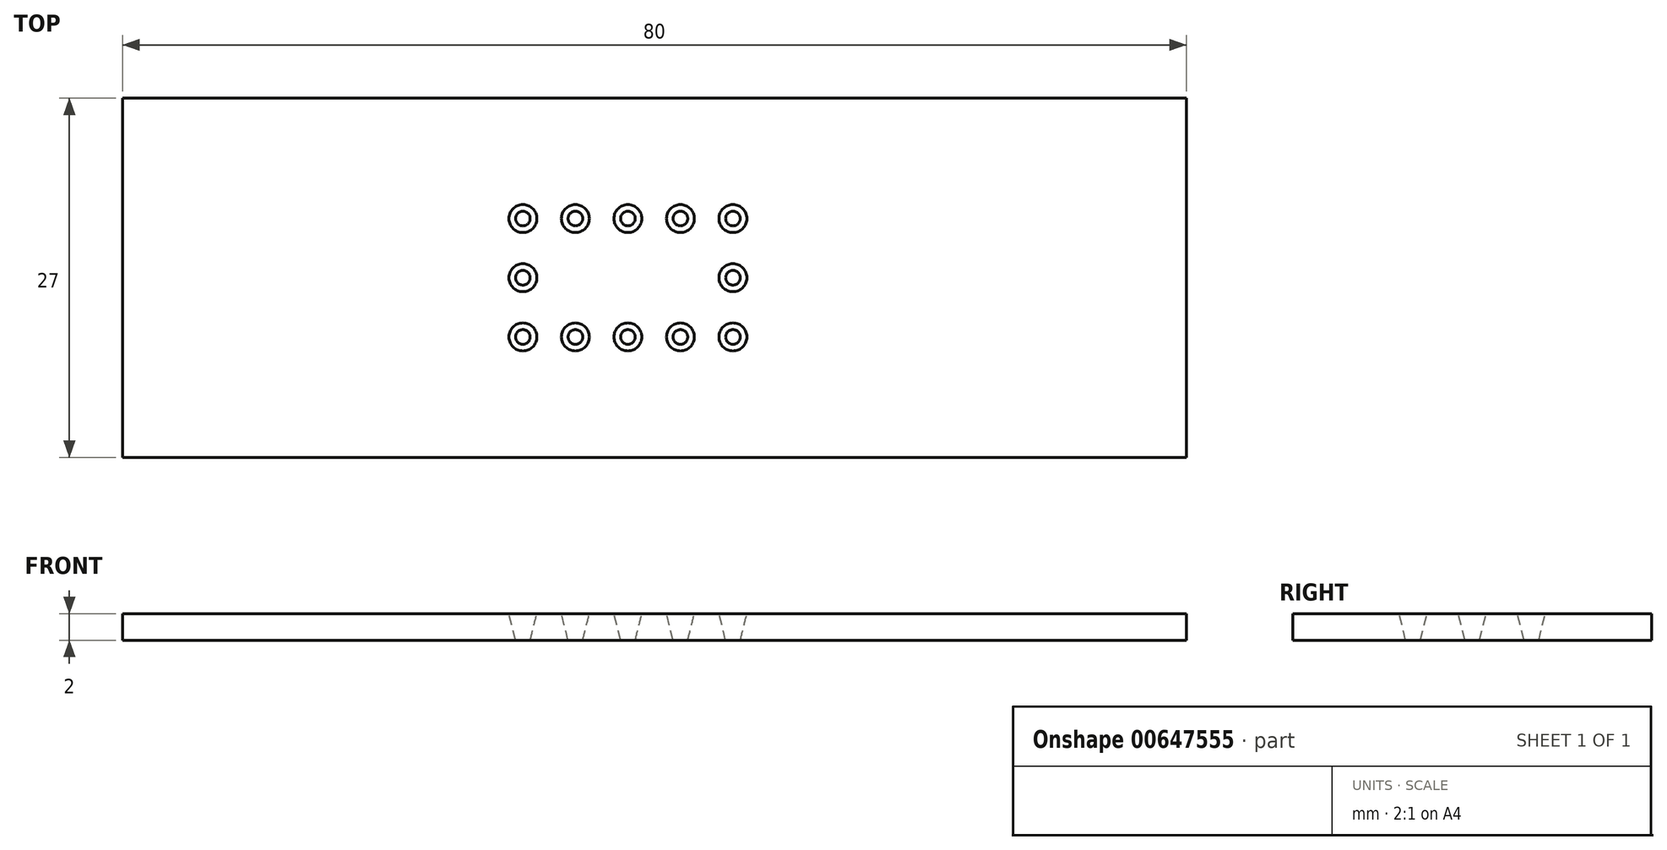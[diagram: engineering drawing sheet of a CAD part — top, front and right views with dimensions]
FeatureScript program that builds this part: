
annotation { "Feature Type Name" : "Feature", "Feature Type Description" : "" }
export const myFeature = defineFeature(function(context is Context, id is Id, definition is map)
    precondition{}
    {
        {
            var Q0;
            Q0=qCreatedBy(makeId("Top.planeOp"),FACE);
            var sketch = newSketch(context, id + "F0", { "sketchPlane" : qUnion([Q0])});
            skLineSegment(sketch, "E0.bottom", {"start": v(40, -13.5) * mm, "end": v(-40, -13.5) * mm});
            skLineSegment(sketch, "E0.top", {"start": v(40, 13.5) * mm, "end": v(-40, 13.5) * mm});
            skLineSegment(sketch, "E0.left", {"start": v(40, -13.5) * mm, "end": v(40, 13.5) * mm});
            skLineSegment(sketch, "E0.right", {"start": v(-40, -13.5) * mm, "end": v(-40, 13.5) * mm});
            skPoint(sketch, "E0.middle", {"position": v(0, 0) * mm});
            skLineSegment(sketch, "E1", {"start": v(-2, 13.5) * mm, "end": v(-2, -13.5) * mm, "construction": true});
            skLineSegment(sketch, "E2.bottom", {"start": v(7.9, -6.45) * mm, "end": v(-11.9, -6.45) * mm, "construction": true});
            skLineSegment(sketch, "E2.top", {"start": v(7.9, 6.45) * mm, "end": v(-11.9, 6.45) * mm, "construction": true});
            skLineSegment(sketch, "E2.left", {"start": v(7.9, -6.45) * mm, "end": v(7.9, 6.45) * mm, "construction": true});
            skLineSegment(sketch, "E2.right", {"start": v(-11.9, -6.45) * mm, "end": v(-11.9, 6.45) * mm, "construction": true});
            skPoint(sketch, "E2.middle", {"position": v(-2, 0) * mm});
            skCircle(sketch, "E3", {"center": v(-9.9, -4.45) * mm, "radius": 2 * mm, "construction": true});
            skCircle(sketch, "E4", {"center": v(-9.9, 4.45) * mm, "radius": 2 * mm, "construction": true});
            skCircle(sketch, "E5", {"center": v(-9.9, 0) * mm, "radius": 2 * mm, "construction": true});
            skCircle(sketch, "E6", {"center": v(5.9, 4.45) * mm, "radius": 2 * mm, "construction": true});
            skCircle(sketch, "E7", {"center": v(5.9, 0) * mm, "radius": 2 * mm, "construction": true});
            skCircle(sketch, "E8", {"center": v(5.9, -4.45) * mm, "radius": 2 * mm, "construction": true});
            skCircle(sketch, "E9", {"center": v(-2, -4.45) * mm, "radius": 2 * mm, "construction": true});
            skCircle(sketch, "E10", {"center": v(-2, 4.45) * mm, "radius": 2 * mm, "construction": true});
            skLineSegment(sketch, "E11", {"start": v(-9.9, 4.45) * mm, "end": v(-2, 4.45) * mm, "construction": true});
            skLineSegment(sketch, "E12", {"start": v(-2, -4.45) * mm, "end": v(5.9, -4.45) * mm, "construction": true});
            skCircle(sketch, "E13", {"center": v(-5.95, 4.45) * mm, "radius": 2 * mm, "construction": true});
            skCircle(sketch, "E14", {"center": v(1.95, 4.45) * mm, "radius": 2 * mm, "construction": true});
            skCircle(sketch, "E15", {"center": v(-5.95, -4.45) * mm, "radius": 2 * mm, "construction": true});
            skCircle(sketch, "E16", {"center": v(1.95, -4.45) * mm, "radius": 2 * mm, "construction": true});
            skSolve(sketch);
        }
        {
            var Q0;
            Q0=makeQuery(id+"F0.imprint","IMPRINT",FACE,{"disambiguationData":[TD([[makeQuery(id+"F0.imprint","IMPRINT",EDGE,{"derivedFrom":sQuery(id+"F0.wireOp",EDGE,"E0.bottom")}),-1.0]])]});
            extrude(context, id + "F1", {"entities" : qUnion([Q0]), "depth" : 2 * mm, "offsetDistance" : 25 * mm});
        }
        {
            var Q0;
            Q0=makeQuery(id+"F1.opExtrude","CAP_FACE",FACE,{"disambiguationData":[OSD([sQuery(id+"F0.wireOp",EDGE,"E0.bottom"),sQuery(id+"F0.wireOp",EDGE,"E0.top"),sQuery(id+"F0.wireOp",EDGE,"E0.left"),sQuery(id+"F0.wireOp",EDGE,"E0.right")])],"isStart":false});
            var sketch = newSketch(context, id + "F2", { "sketchPlane" : qUnion([Q0])});
            skPoint(sketch, "E17.0", {"position": v(-9.9, 4.45) * mm});
            skPoint(sketch, "E18.0", {"position": v(-5.95, 4.45) * mm});
            skPoint(sketch, "E19.0", {"position": v(-2, 4.45) * mm});
            skPoint(sketch, "E20.0", {"position": v(1.95, 4.45) * mm});
            skPoint(sketch, "E21.0", {"position": v(5.9, 4.45) * mm});
            skPoint(sketch, "E22.0", {"position": v(5.9, 0) * mm});
            skPoint(sketch, "E23.0", {"position": v(5.9, -4.45) * mm});
            skPoint(sketch, "E24.0", {"position": v(1.95, -4.45) * mm});
            skPoint(sketch, "E25.0", {"position": v(-2, -4.45) * mm});
            skPoint(sketch, "E26.0", {"position": v(-5.95, -4.45) * mm});
            skPoint(sketch, "E27.0", {"position": v(-9.9, -4.45) * mm});
            skPoint(sketch, "E28.0", {"position": v(-9.9, 0) * mm});
            skCircle(sketch, "E29", {"center": v(-9.9, 4.45) * mm, "radius": 1.05 * mm});
            skCircle(sketch, "E30", {"center": v(-5.95, 4.45) * mm, "radius": 1.05 * mm});
            skCircle(sketch, "E31", {"center": v(-2, 4.45) * mm, "radius": 1.05 * mm});
            skCircle(sketch, "E32", {"center": v(-9.9, 0) * mm, "radius": 1.05 * mm});
            skCircle(sketch, "E33", {"center": v(-9.9, -4.45) * mm, "radius": 1.05 * mm});
            skCircle(sketch, "E34", {"center": v(-5.95, -4.45) * mm, "radius": 1.05 * mm});
            skCircle(sketch, "E35", {"center": v(-2, -4.45) * mm, "radius": 1.05 * mm});
            skCircle(sketch, "E36", {"center": v(1.95, -4.45) * mm, "radius": 1.05 * mm});
            skCircle(sketch, "E37", {"center": v(5.9, -4.45) * mm, "radius": 1.05 * mm});
            skCircle(sketch, "E38", {"center": v(5.9, 0) * mm, "radius": 1.05 * mm});
            skCircle(sketch, "E39", {"center": v(5.9, 4.45) * mm, "radius": 1.05 * mm});
            skCircle(sketch, "E40", {"center": v(1.95, 4.45) * mm, "radius": 1.05 * mm});
            skSolve(sketch);
        }
        {
            var Q0;
            Q0=makeQuery(id+"F2.imprint","IMPRINT",FACE,{"disambiguationData":[TD([[makeQuery(id+"F2.imprint","IMPRINT",EDGE,{"derivedFrom":sQuery(id+"F2.wireOp",EDGE,"E29")}),1.0]])]});
            var Q1;
            Q1=makeQuery(id+"F2.imprint","IMPRINT",FACE,{"disambiguationData":[TD([[makeQuery(id+"F2.imprint","IMPRINT",EDGE,{"derivedFrom":sQuery(id+"F2.wireOp",EDGE,"E30")}),1.0]])]});
            var Q2;
            Q2=makeQuery(id+"F2.imprint","IMPRINT",FACE,{"disambiguationData":[TD([[makeQuery(id+"F2.imprint","IMPRINT",EDGE,{"derivedFrom":sQuery(id+"F2.wireOp",EDGE,"E31")}),1.0]])]});
            var Q3;
            Q3=makeQuery(id+"F2.imprint","IMPRINT",FACE,{"disambiguationData":[TD([[makeQuery(id+"F2.imprint","IMPRINT",EDGE,{"derivedFrom":sQuery(id+"F2.wireOp",EDGE,"E40")}),1.0]])]});
            var Q4;
            Q4=makeQuery(id+"F2.imprint","IMPRINT",FACE,{"disambiguationData":[TD([[makeQuery(id+"F2.imprint","IMPRINT",EDGE,{"derivedFrom":sQuery(id+"F2.wireOp",EDGE,"E39")}),1.0]])]});
            var Q5;
            Q5=makeQuery(id+"F2.imprint","IMPRINT",FACE,{"disambiguationData":[TD([[makeQuery(id+"F2.imprint","IMPRINT",EDGE,{"derivedFrom":sQuery(id+"F2.wireOp",EDGE,"E32")}),1.0]])]});
            var Q6;
            Q6=makeQuery(id+"F2.imprint","IMPRINT",FACE,{"disambiguationData":[TD([[makeQuery(id+"F2.imprint","IMPRINT",EDGE,{"derivedFrom":sQuery(id+"F2.wireOp",EDGE,"E34")}),1.0]])]});
            var Q7;
            Q7=makeQuery(id+"F2.imprint","IMPRINT",FACE,{"disambiguationData":[TD([[makeQuery(id+"F2.imprint","IMPRINT",EDGE,{"derivedFrom":sQuery(id+"F2.wireOp",EDGE,"E35")}),1.0]])]});
            var Q8;
            Q8=makeQuery(id+"F2.imprint","IMPRINT",FACE,{"disambiguationData":[TD([[makeQuery(id+"F2.imprint","IMPRINT",EDGE,{"derivedFrom":sQuery(id+"F2.wireOp",EDGE,"E33")}),1.0]])]});
            var Q9;
            Q9=makeQuery(id+"F2.imprint","IMPRINT",FACE,{"disambiguationData":[TD([[makeQuery(id+"F2.imprint","IMPRINT",EDGE,{"derivedFrom":sQuery(id+"F2.wireOp",EDGE,"E36")}),1.0]])]});
            var Q10;
            Q10=makeQuery(id+"F2.imprint","IMPRINT",FACE,{"disambiguationData":[TD([[makeQuery(id+"F2.imprint","IMPRINT",EDGE,{"derivedFrom":sQuery(id+"F2.wireOp",EDGE,"E37")}),1.0]])]});
            var Q11;
            Q11=makeQuery(id+"F2.imprint","IMPRINT",FACE,{"disambiguationData":[TD([[makeQuery(id+"F2.imprint","IMPRINT",EDGE,{"derivedFrom":sQuery(id+"F2.wireOp",EDGE,"E38")}),1.0]])]});
            extrude(context, id + "F3", {"entities" : qUnion([Q0, Q1, Q2, Q3, Q4, Q5, Q6, Q7, Q8, Q9, Q10, Q11]), "operationType" : NewBodyOperationType.REMOVE, "oppositeDirection" : true, "depth" : 25 * mm, "offsetDistance" : 25 * mm, "hasDraft" : true, "draftAngle" : 14 * degree, "draftPullDirection" : true});
        }
    });
